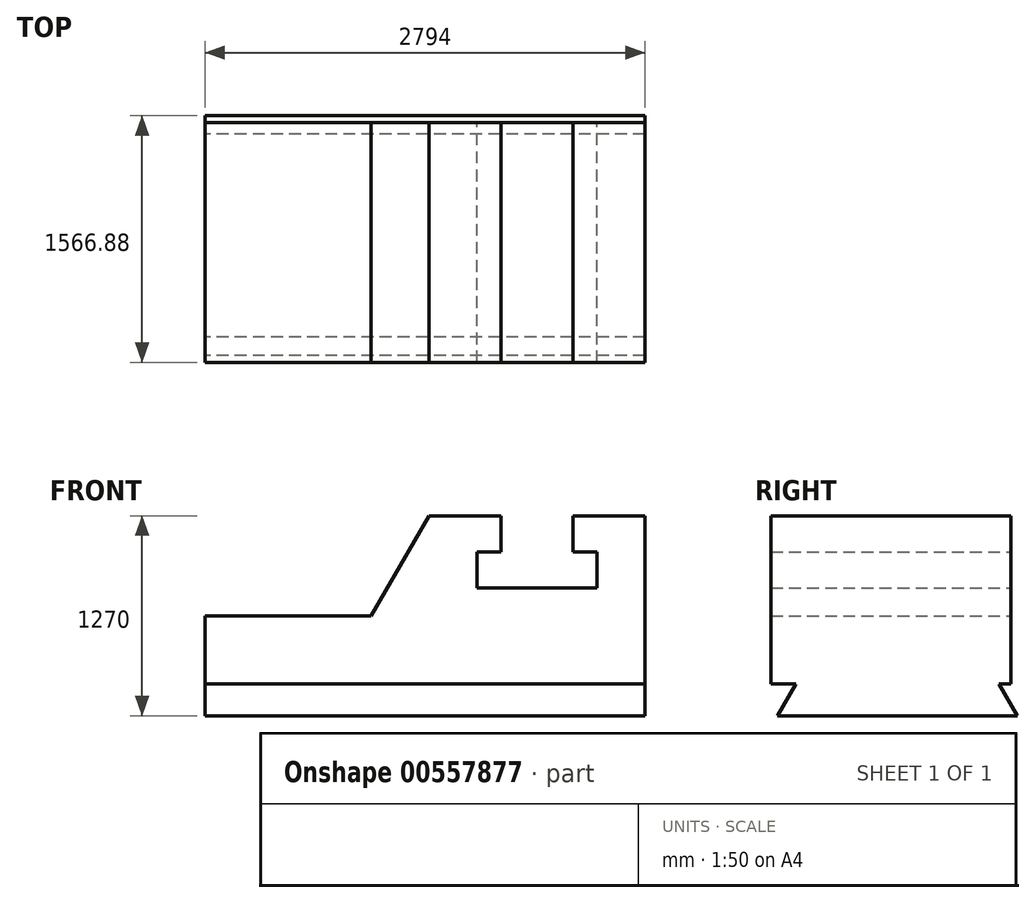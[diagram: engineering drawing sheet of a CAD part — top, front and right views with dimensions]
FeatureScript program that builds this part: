
annotation { "Feature Type Name" : "Feature", "Feature Type Description" : "" }
export const myFeature = defineFeature(function(context is Context, id is Id, definition is map)
    precondition{}
    {
        {
            var Q0;
            Q0=qCreatedBy(makeId("Front.planeOp"),FACE);
            var sketch = newSketch(context, id + "F0", { "sketchPlane" : qUnion([Q0])});
            skLineSegment(sketch, "E0", {"start": v(-146.88, -75.08) * mm, "end": v(2647.12, -75.08) * mm});
            skLineSegment(sketch, "E1", {"start": v(2647.12, -75.08) * mm, "end": v(2647.12, 991.72) * mm});
            skLineSegment(sketch, "E2", {"start": v(2647.12, 991.72) * mm, "end": v(2189.92, 991.72) * mm});
            skLineSegment(sketch, "E3", {"start": v(2189.92, 991.72) * mm, "end": v(2189.92, 763.12) * mm});
            skLineSegment(sketch, "E4", {"start": v(2189.92, 763.12) * mm, "end": v(2342.32, 763.12) * mm});
            skLineSegment(sketch, "E5", {"start": v(2342.32, 763.12) * mm, "end": v(2342.32, 534.52) * mm});
            skLineSegment(sketch, "E6", {"start": v(2342.32, 534.52) * mm, "end": v(1580.32, 534.52) * mm});
            skLineSegment(sketch, "E7", {"start": v(1580.32, 534.52) * mm, "end": v(1580.32, 763.12) * mm});
            skLineSegment(sketch, "E8", {"start": v(1580.32, 763.12) * mm, "end": v(1732.72, 763.12) * mm});
            skLineSegment(sketch, "E9", {"start": v(1732.72, 763.12) * mm, "end": v(1732.72, 991.72) * mm});
            skLineSegment(sketch, "E10", {"start": v(1732.72, 991.72) * mm, "end": v(1275.52, 991.72) * mm});
            skLineSegment(sketch, "E11", {"start": v(-146.88, -75.08) * mm, "end": v(-146.88, 356.72) * mm});
            skLineSegment(sketch, "E12", {"start": v(1275.52, 991.72) * mm, "end": v(908.9, 356.72) * mm});
            skLineSegment(sketch, "E13", {"start": v(908.9, 356.72) * mm, "end": v(-146.88, 356.72) * mm});
            skSolve(sketch);
        }
        {
            var Q0;
            Q0=makeQuery(id+"F0.imprint","IMPRINT",FACE,{"disambiguationData":[TD([[makeQuery(id+"F0.imprint","IMPRINT",EDGE,{"derivedFrom":sQuery(id+"F0.wireOp",EDGE,"E0")}),1.0]])]});
            extrude(context, id + "F1", {"entities" : qUnion([Q0]), "depth" : 1524 * mm, "offsetDistance" : 25.4 * mm});
        }
        {
            var Q0;
            Q0=makeQuery(id+"F1.opExtrude","SWEPT_FACE",FACE,{"disambiguationData":[OSD([sQuery(id+"F0.wireOp",EDGE,"E11")])]});
            var sketch = newSketch(context, id + "F2", { "sketchPlane" : qUnion([Q0])});
            skLineSegment(sketch, "E14", {"start": v(1481.12, -278.28) * mm, "end": v(-42.88, -278.28) * mm});
            skLineSegment(sketch, "E15", {"start": v(0, -75.08) * mm, "end": v(74.44, -75.08) * mm});
            skLineSegment(sketch, "E16", {"start": v(74.44, -75.08) * mm, "end": v(-42.88, -278.28) * mm});
            skLineSegment(sketch, "E17", {"start": v(1524, -75.08) * mm, "end": v(1363.8, -75.08) * mm});
            skLineSegment(sketch, "E18", {"start": v(1363.8, -75.08) * mm, "end": v(1481.12, -278.28) * mm});
            skSolve(sketch);
        }
        {
            var Q0;
            Q0 = qSketchRegion(id + "F2", true);
            var Q1;
            Q1=makeQuery(id+"F2.imprint","IMPRINT",FACE,{"disambiguationData":[TD([[makeQuery(id+"F2.imprint","IMPRINT",EDGE,{"derivedFrom":sQuery(id+"F2.wireOp",EDGE,"E14")}),-1.0]])]});
            extrude(context, id + "F3", {"entities" : qUnion([Q0, Q1]), "operationType" : NewBodyOperationType.ADD, "oppositeDirection" : true, "depth" : 2794 * mm, "offsetDistance" : 25.4 * mm});
        }
    });
